# Revit family: Valvula_DeControl_ChequeCortina_Grival
name_source: partatom
category: Pipe Accessories
units: mm (PartAtom-declared; Revit-internal decimal feet)

## family parameters
Always vertical = Yes
Cut with Voids When Loaded = No
OmniClass Number = 23.27.31.13.19
OmniClass Title = Check Balancing Valves
Part Type = Valve - Breaks Into
Round Connector Dimension = Use Diameter
Shared = No
Work Plane-Based = No

## types (3) — shared parameters
4 = 2 mm  [stored 0.00656168 ft]
Alto Calc = 1 mm  [stored 0.00328084 ft]
Ancho Calc = 1 mm  [stored 0.00328084 ft]
Creado por = BIMBAU
Description = Permite el paso de agua en una dirección, evitando el flujo en la dirección opuesta.
Fecha de creación = 12/03/2021
Manufacturer = Grival
Model = Cheque cortina
Presión de servicio = Presión de trabajo manométrica máxima del agua 1034 kPa (150 psi) - Presión mínima recomendada 138 kPa (20 psi).
Recubrimientos = Resistente a la corrosión. Condición de servicio recomendada, uso doméstico e institucional.
Temperatura de uso = De 4° C A 16° C (40° F y 61° F).
URL = https://www.grival.com
c = 2 mm  [stored 0.00656168 ft]
zero-valued in all types: Cost, Default Elevation

## per-type parameters (varying)
| type | 1 | 2 | 3 | 5 | Conector Offset | Conexión | D | DN | H | Hex | Inch | L | L2 | Material | Peso | Rad | T1 | T2 | a | b | mm |
| 797150001 (1/2") | 3 mm  [stored 0.00984252 ft] | 5 mm  [stored 0.0164042 ft] | 3 mm  [stored 0.00984252 ft] | 6 mm  [stored 0.019685 ft] | 9 mm | 15 mm  [stored 0.0492126 ft] | 13 mm | 15 | 33 mm  [stored 0.108268 ft] | 29 mm  [stored 0.0951444 ft] | 1/2 | 48 mm  [stored 0.15748 ft] | 15 mm  [stored 0.0492126 ft] | Corona_Bronce | 0.15 Kgs | 38 mm | 12 mm  [stored 0.0393701 ft] | 10 mm  [stored 0.0328084 ft] | 10 mm  [stored 0.0328084 ft] | 2 mm  [stored 0.00656168 ft] | 13 mm |
| 797160001 (3/4") | 3 mm  [stored 0.00984252 ft] | 6 mm  [stored 0.019685 ft] | 3 mm  [stored 0.00984252 ft] | 7 mm  [stored 0.0229659 ft] | 10 mm  [stored 0.0328084 ft] | 20 mm  [stored 0.0656168 ft] | 18 mm  [stored 0.0590551 ft] | 20 | 37 mm  [stored 0.121391 ft] | 36 mm | 3/4 | 53 mm  [stored 0.173885 ft] | 17 mm | Corona_Bronce | 0.22 Kgs | 43 mm | 13 mm | 13 mm | 12 mm  [stored 0.0393701 ft] | 3 mm  [stored 0.00984252 ft] | 20 mm  [stored 0.0656168 ft] |
| 797170001 (1") | 4 mm  [stored 0.0131234 ft] | 7 mm  [stored 0.0229659 ft] | 4 mm  [stored 0.0131234 ft] | 8 mm  [stored 0.0262467 ft] | 11 mm | 25 mm  [stored 0.082021 ft] | 22 mm  [stored 0.0721785 ft] | 25 | 43 mm | 43 mm | 1 | 62 mm  [stored 0.203412 ft] | 20 mm  [stored 0.0656168 ft] | Brass | 0.35 Kgs | 50 mm  [stored 0.164042 ft] | 13 mm | 13 mm | 13 mm | 3 mm  [stored 0.00984252 ft] | 25 mm  [stored 0.082021 ft] |

note: [stored X ft] marks values corroborated as IEEE doubles in the binary element streams (Revit-internal decimal feet)

## geometry (parser evidence)
native form markers: Sweep x4
no freeform markers — native parametric forms only
